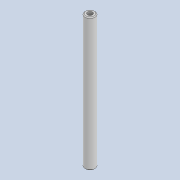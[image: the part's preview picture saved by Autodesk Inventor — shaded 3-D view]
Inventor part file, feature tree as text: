
AUTODESK INVENTOR PART (.ipt)
format: ipt  version: 2020 (Build 240168000, 168)  size: 80,896 bytes
history: native  units: mm
features: extrude x2, sketch x2, chamfer x1
ambient origin geometry x8: Origin, YZ Plane, XZ Plane, XY Plane, X Axis, Y Axis, Z Axis, Center Point
bodies: Solid1 (feature_tree)
feature tree (5):
  extrude  "Extrusion1"  Depth=40.0mm TaperAngle=0.0deg
  extrude  "Extrusion2"  Depth=40.0mm TaperAngle=0.0deg
  chamfer  "Chamfer1"  Distance=0.25mm Angle=45.0deg
  sketch  "Sketch1"  dims[d0=3.0mm d1=40.0mm d2=0.0mm]
  sketch  "Sketch2"  dims[d3=1.5mm d4=40.0mm d5=0.0mm d6=0.25mm d7=2.0mm d8=45.0deg]
